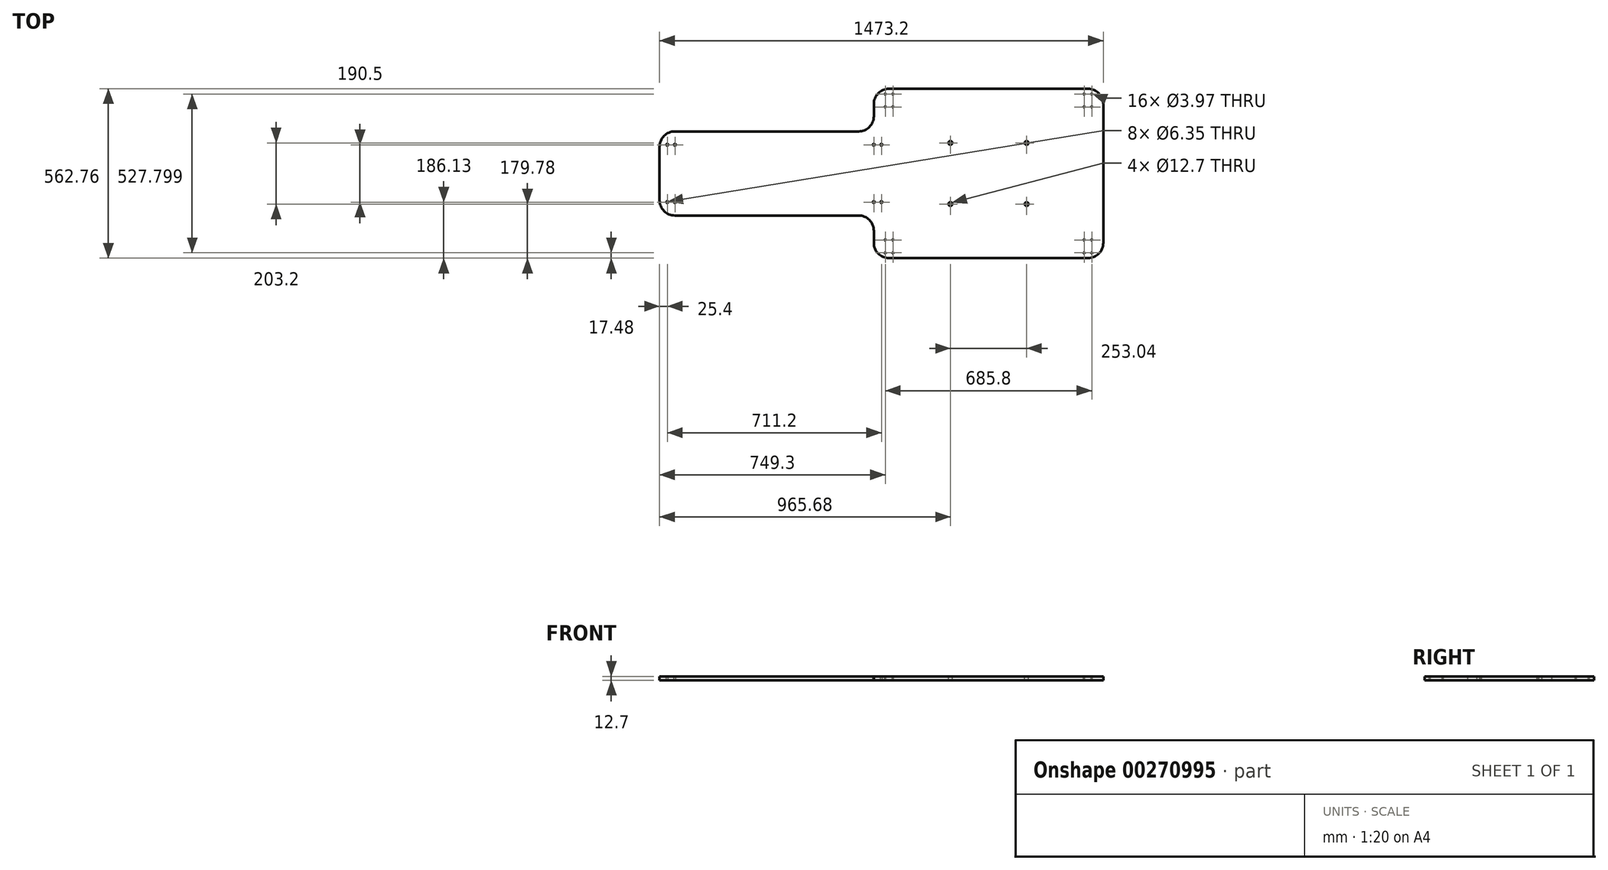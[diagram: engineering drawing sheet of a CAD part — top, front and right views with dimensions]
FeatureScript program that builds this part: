
annotation { "Feature Type Name" : "Feature", "Feature Type Description" : "" }
export const myFeature = defineFeature(function(context is Context, id is Id, definition is map)
    precondition{}
    {
        {
            var Q0;
            Q0=qCreatedBy(makeId("Top.planeOp"),FACE);
            var sketch = newSketch(context, id + "F0", { "sketchPlane" : qUnion([Q0])});
            skLineSegment(sketch, "E0", {"start": v(0, 0) * mm, "end": v(1473.2, 0) * mm, "construction": true});
            skLineSegment(sketch, "E1", {"start": v(1473.2, 0) * mm, "end": v(1473.2, 230.58) * mm});
            skLineSegment(sketch, "E2", {"start": v(1422.4, 281.38) * mm, "end": v(762, 281.38) * mm});
            skLineSegment(sketch, "E3", {"start": v(711.2, 230.58) * mm, "end": v(711.2, 190.5) * mm});
            skLineSegment(sketch, "E4", {"start": v(660.4, 139.7) * mm, "end": v(50.8, 139.7) * mm});
            skLineSegment(sketch, "E5", {"start": v(0, 88.9) * mm, "end": v(0, 0) * mm});
            skPoint(sketch, "E6.visualSharp", {"position": v(0, 139.7) * mm});
            skArc(sketch, "E6.filletArc", {"start": v(50.8, 139.7) * mm, "mid": v(14.88, 124.82) * mm, "end": v(0, 88.9) * mm});
            skPoint(sketch, "E7.visualSharp", {"position": v(711.2, 281.38) * mm});
            skArc(sketch, "E7.filletArc", {"start": v(762, 281.38) * mm, "mid": v(726.08, 266.5) * mm, "end": v(711.2, 230.58) * mm});
            skPoint(sketch, "E8.visualSharp", {"position": v(711.2, 139.7) * mm});
            skArc(sketch, "E8.filletArc", {"start": v(660.4, 139.7) * mm, "mid": v(696.32, 154.58) * mm, "end": v(711.2, 190.5) * mm});
            skPoint(sketch, "E9.visualSharp", {"position": v(1473.2, 281.38) * mm});
            skArc(sketch, "E9.filletArc", {"start": v(1473.2, 230.58) * mm, "mid": v(1458.32, 266.5) * mm, "end": v(1422.4, 281.38) * mm});
            skPoint(sketch, "E10.MirrorP", {"position": v(711.2, -139.7) * mm});
            skPoint(sketch, "E11.MirrorP", {"position": v(711.2, -281.38) * mm});
            skLineSegment(sketch, "E12.MirrorCS", {"start": v(1473.2, 0) * mm, "end": v(1473.2, -230.58) * mm});
            skLineSegment(sketch, "E13.MirrorCS", {"start": v(1422.4, -281.38) * mm, "end": v(762, -281.38) * mm});
            skPoint(sketch, "E14.MirrorP", {"position": v(0, -139.7) * mm});
            skLineSegment(sketch, "E15.MirrorCS", {"start": v(711.2, -230.58) * mm, "end": v(711.2, -190.5) * mm});
            skPoint(sketch, "E16.MirrorP", {"position": v(1473.2, -281.38) * mm});
            skArc(sketch, "E17.MirrorCS", {"start": v(1473.2, -230.58) * mm, "mid": v(1458.32, -266.5) * mm, "end": v(1422.4, -281.38) * mm});
            skLineSegment(sketch, "E18.MirrorCS", {"start": v(0, -88.9) * mm, "end": v(0, 0) * mm});
            skArc(sketch, "E19.MirrorCS", {"start": v(660.4, -139.7) * mm, "mid": v(696.32, -154.58) * mm, "end": v(711.2, -190.5) * mm});
            skLineSegment(sketch, "E20.MirrorCS", {"start": v(660.4, -139.7) * mm, "end": v(50.8, -139.7) * mm});
            skArc(sketch, "E21.MirrorCS", {"start": v(50.8, -139.7) * mm, "mid": v(14.88, -124.82) * mm, "end": v(0, -88.9) * mm});
            skArc(sketch, "E22.MirrorCS", {"start": v(762, -281.38) * mm, "mid": v(726.08, -266.5) * mm, "end": v(711.2, -230.58) * mm});
            skPoint(sketch, "E23", {"position": v(1473.2, 244.48) * mm});
            skLineSegment(sketch, "E24", {"start": v(1473.2, 244.48) * mm, "end": v(1246.97, 244.48) * mm, "construction": true});
            skSolve(sketch);
        }
        {
            var Q0;
            Q0=makeQuery(id+"F0.imprint","IMPRINT",FACE,{"disambiguationData":[TD([[makeQuery(id+"F0.imprint","IMPRINT",EDGE,{"derivedFrom":sQuery(id+"F0.wireOp",EDGE,"E1")}),1.0]])]});
            extrude(context, id + "F1", {"entities" : qUnion([Q0]), "depth" : 12.7 * mm});
        }
        {
            var Q0;
            Q0=makeQuery(id+"F1.opExtrude","CAP_FACE",FACE,{"disambiguationData":[OSD([sQuery(id+"F0.wireOp",EDGE,"E1"),sQuery(id+"F0.wireOp",EDGE,"E2"),sQuery(id+"F0.wireOp",EDGE,"E3"),sQuery(id+"F0.wireOp",EDGE,"E4"),sQuery(id+"F0.wireOp",EDGE,"E5"),sQuery(id+"F0.wireOp",EDGE,"E6.filletArc"),sQuery(id+"F0.wireOp",EDGE,"E7.filletArc"),sQuery(id+"F0.wireOp",EDGE,"E8.filletArc"),sQuery(id+"F0.wireOp",EDGE,"E9.filletArc"),sQuery(id+"F0.wireOp",EDGE,"E12.MirrorCS"),sQuery(id+"F0.wireOp",EDGE,"E13.MirrorCS"),sQuery(id+"F0.wireOp",EDGE,"E15.MirrorCS"),sQuery(id+"F0.wireOp",EDGE,"E17.MirrorCS"),sQuery(id+"F0.wireOp",EDGE,"E18.MirrorCS"),sQuery(id+"F0.wireOp",EDGE,"E19.MirrorCS"),sQuery(id+"F0.wireOp",EDGE,"E20.MirrorCS"),sQuery(id+"F0.wireOp",EDGE,"E21.MirrorCS"),sQuery(id+"F0.wireOp",EDGE,"E22.MirrorCS")])],"isStart":false});
            var sketch = newSketch(context, id + "F2", { "sketchPlane" : qUnion([Q0])});
            skPoint(sketch, "E25", {"position": v(1422.4, -242.47) * mm});
            skLineSegment(sketch, "E26", {"start": v(1400.97, -242.47) * mm, "end": v(1485.34, -242.47) * mm, "construction": true});
            skLineSegment(sketch, "E27", {"start": v(1422.4, -204.1) * mm, "end": v(1422.4, -307.94) * mm, "construction": true});
            skLineSegment(sketch, "E28", {"start": v(1400.97, -217.07) * mm, "end": v(1443.83, -217.07) * mm, "construction": true});
            skLineSegment(sketch, "E29", {"start": v(1400.97, -267.87) * mm, "end": v(1443.83, -267.87) * mm, "construction": true});
            skPoint(sketch, "E30", {"position": v(1435.1, -263.9) * mm});
            skPoint(sketch, "E31.MirrorP", {"position": v(1435.1, -221.04) * mm});
            skPoint(sketch, "E32.MirrorP", {"position": v(1409.7, -221.04) * mm});
            skPoint(sketch, "E33.MirrorP", {"position": v(1409.7, -263.9) * mm});
            skLineSegment(sketch, "E34", {"start": v(1092.2, 339.37) * mm, "end": v(1092.2, -479.33) * mm, "construction": true});
            skLineSegment(sketch, "E35", {"start": v(1473.2, 0) * mm, "end": v(0, 0) * mm, "construction": true});
            skPoint(sketch, "E36.MirrorP", {"position": v(1409.7, 221.04) * mm});
            skPoint(sketch, "E37.MirrorP", {"position": v(1435.1, 221.04) * mm});
            skPoint(sketch, "E38.MirrorP", {"position": v(1435.1, 263.9) * mm});
            skPoint(sketch, "E39.MirrorP", {"position": v(1409.7, 263.9) * mm});
            skPoint(sketch, "E40.MirrorP", {"position": v(774.7, 263.9) * mm});
            skPoint(sketch, "E41.MirrorP", {"position": v(749.3, 263.9) * mm});
            skPoint(sketch, "E42.MirrorP", {"position": v(749.3, 221.04) * mm});
            skPoint(sketch, "E43.MirrorP", {"position": v(774.7, 221.04) * mm});
            skPoint(sketch, "E44.MirrorP", {"position": v(774.7, -221.04) * mm});
            skPoint(sketch, "E45.MirrorP", {"position": v(749.3, -221.04) * mm});
            skPoint(sketch, "E46.MirrorP", {"position": v(749.3, -263.9) * mm});
            skPoint(sketch, "E47.MirrorP", {"position": v(774.7, -263.9) * mm});
            skPoint(sketch, "E48", {"position": v(1218.72, 101.6) * mm});
            skPoint(sketch, "E49.MirrorP", {"position": v(965.68, 101.6) * mm});
            skPoint(sketch, "E50.MirrorP", {"position": v(1218.72, -101.6) * mm});
            skPoint(sketch, "E51.MirrorP", {"position": v(965.68, -101.6) * mm});
            skPoint(sketch, "E52", {"position": v(25.4, 95.25) * mm});
            skPoint(sketch, "E53", {"position": v(50.8, 95.25) * mm});
            skPoint(sketch, "E54.MirrorP", {"position": v(25.4, -95.25) * mm});
            skPoint(sketch, "E55.MirrorP", {"position": v(50.8, -95.25) * mm});
            skLineSegment(sketch, "E56", {"start": v(381, 211.87) * mm, "end": v(381, -230.79) * mm, "construction": true});
            skPoint(sketch, "E57.MirrorP", {"position": v(711.2, 95.25) * mm});
            skPoint(sketch, "E58.MirrorP", {"position": v(736.6, 95.25) * mm});
            skPoint(sketch, "E59.MirrorP", {"position": v(736.6, -95.25) * mm});
            skPoint(sketch, "E60.MirrorP", {"position": v(711.2, -95.25) * mm});
            skSolve(sketch);
        }
        {
            var Q0;
            Q0=sQuery(id+"F2.wireOp",VERTEX,"E41.MirrorP");
            var Q1;
            Q1=sQuery(id+"F2.wireOp",VERTEX,"E40.MirrorP");
            var Q2;
            Q2=sQuery(id+"F2.wireOp",VERTEX,"E43.MirrorP");
            var Q3;
            Q3=sQuery(id+"F2.wireOp",VERTEX,"E42.MirrorP");
            var Q4;
            Q4=sQuery(id+"F2.wireOp",VERTEX,"E45.MirrorP");
            var Q5;
            Q5=sQuery(id+"F2.wireOp",VERTEX,"E44.MirrorP");
            var Q6;
            Q6=sQuery(id+"F2.wireOp",VERTEX,"E47.MirrorP");
            var Q7;
            Q7=sQuery(id+"F2.wireOp",VERTEX,"E46.MirrorP");
            var Q8;
            Q8=sQuery(id+"F2.wireOp",VERTEX,"E32.MirrorP");
            var Q9;
            Q9=sQuery(id+"F2.wireOp",VERTEX,"E31.MirrorP");
            var Q10;
            Q10=sQuery(id+"F2.wireOp",VERTEX,"E30");
            var Q11;
            Q11=sQuery(id+"F2.wireOp",VERTEX,"E33.MirrorP");
            var Q12;
            Q12=sQuery(id+"F2.wireOp",VERTEX,"E37.MirrorP");
            var Q13;
            Q13=sQuery(id+"F2.wireOp",VERTEX,"E36.MirrorP");
            var Q14;
            Q14=sQuery(id+"F2.wireOp",VERTEX,"E39.MirrorP");
            var Q15;
            Q15=sQuery(id+"F2.wireOp",VERTEX,"E38.MirrorP");
            var Q16;
            Q16=makeQuery(id+"F1.opExtrude","SWEPT_BODY",BODY,{"disambiguationData":[OSD([sQuery(id+"F0.wireOp",EDGE,"E1"),sQuery(id+"F0.wireOp",EDGE,"E2"),sQuery(id+"F0.wireOp",EDGE,"E3"),sQuery(id+"F0.wireOp",EDGE,"E4"),sQuery(id+"F0.wireOp",EDGE,"E5"),sQuery(id+"F0.wireOp",EDGE,"E6.filletArc"),sQuery(id+"F0.wireOp",EDGE,"E7.filletArc"),sQuery(id+"F0.wireOp",EDGE,"E8.filletArc"),sQuery(id+"F0.wireOp",EDGE,"E9.filletArc"),sQuery(id+"F0.wireOp",EDGE,"E12.MirrorCS"),sQuery(id+"F0.wireOp",EDGE,"E13.MirrorCS"),sQuery(id+"F0.wireOp",EDGE,"E15.MirrorCS"),sQuery(id+"F0.wireOp",EDGE,"E17.MirrorCS"),sQuery(id+"F0.wireOp",EDGE,"E18.MirrorCS"),sQuery(id+"F0.wireOp",EDGE,"E19.MirrorCS"),sQuery(id+"F0.wireOp",EDGE,"E20.MirrorCS"),sQuery(id+"F0.wireOp",EDGE,"E21.MirrorCS"),sQuery(id+"F0.wireOp",EDGE,"E22.MirrorCS")])]});
            hole(context, id + "F3", {"style" : HoleStyle.SIMPLE, "endStyle" : HoleEndStyle.THROUGH, "holeDiameter" : 3.97 * mm, "tappedDepth" : 12.7 * mm, "tapClearance" : 3, "locations" : qUnion([Q0, Q1, Q2, Q3, Q4, Q5, Q6, Q7, Q8, Q9, Q10, Q11, Q12, Q13, Q14, Q15]), "scope" : qUnion([Q16])});
        }
        {
            var Q0;
            Q0=sQuery(id+"F2.wireOp",VERTEX,"E49.MirrorP");
            var Q1;
            Q1=sQuery(id+"F2.wireOp",VERTEX,"E48");
            var Q2;
            Q2=sQuery(id+"F2.wireOp",VERTEX,"E50.MirrorP");
            var Q3;
            Q3=sQuery(id+"F2.wireOp",VERTEX,"E51.MirrorP");
            var Q4;
            Q4=makeQuery(id+"F1.opExtrude","SWEPT_BODY",BODY,{"disambiguationData":[OSD([sQuery(id+"F0.wireOp",EDGE,"E1"),sQuery(id+"F0.wireOp",EDGE,"E2"),sQuery(id+"F0.wireOp",EDGE,"E3"),sQuery(id+"F0.wireOp",EDGE,"E4"),sQuery(id+"F0.wireOp",EDGE,"E5"),sQuery(id+"F0.wireOp",EDGE,"E6.filletArc"),sQuery(id+"F0.wireOp",EDGE,"E7.filletArc"),sQuery(id+"F0.wireOp",EDGE,"E8.filletArc"),sQuery(id+"F0.wireOp",EDGE,"E9.filletArc"),sQuery(id+"F0.wireOp",EDGE,"E12.MirrorCS"),sQuery(id+"F0.wireOp",EDGE,"E13.MirrorCS"),sQuery(id+"F0.wireOp",EDGE,"E15.MirrorCS"),sQuery(id+"F0.wireOp",EDGE,"E17.MirrorCS"),sQuery(id+"F0.wireOp",EDGE,"E18.MirrorCS"),sQuery(id+"F0.wireOp",EDGE,"E19.MirrorCS"),sQuery(id+"F0.wireOp",EDGE,"E20.MirrorCS"),sQuery(id+"F0.wireOp",EDGE,"E21.MirrorCS"),sQuery(id+"F0.wireOp",EDGE,"E22.MirrorCS")])]});
            hole(context, id + "F4", {"style" : HoleStyle.SIMPLE, "endStyle" : HoleEndStyle.THROUGH, "holeDiameter" : 12.7 * mm, "tappedDepth" : 12.7 * mm, "tapClearance" : 3, "locations" : qUnion([Q0, Q1, Q2, Q3]), "scope" : qUnion([Q4])});
        }
        {
            var Q0;
            Q0=sQuery(id+"F2.wireOp",VERTEX,"E52");
            var Q1;
            Q1=sQuery(id+"F2.wireOp",VERTEX,"E53");
            var Q2;
            Q2=sQuery(id+"F2.wireOp",VERTEX,"E55.MirrorP");
            var Q3;
            Q3=sQuery(id+"F2.wireOp",VERTEX,"E54.MirrorP");
            var Q4;
            Q4=sQuery(id+"F2.wireOp",VERTEX,"E57.MirrorP");
            var Q5;
            Q5=sQuery(id+"F2.wireOp",VERTEX,"E58.MirrorP");
            var Q6;
            Q6=sQuery(id+"F2.wireOp",VERTEX,"E59.MirrorP");
            var Q7;
            Q7=sQuery(id+"F2.wireOp",VERTEX,"E60.MirrorP");
            var Q8;
            Q8=makeQuery(id+"F1.opExtrude","SWEPT_BODY",BODY,{"disambiguationData":[OSD([sQuery(id+"F0.wireOp",EDGE,"E1"),sQuery(id+"F0.wireOp",EDGE,"E2"),sQuery(id+"F0.wireOp",EDGE,"E3"),sQuery(id+"F0.wireOp",EDGE,"E4"),sQuery(id+"F0.wireOp",EDGE,"E5"),sQuery(id+"F0.wireOp",EDGE,"E6.filletArc"),sQuery(id+"F0.wireOp",EDGE,"E7.filletArc"),sQuery(id+"F0.wireOp",EDGE,"E8.filletArc"),sQuery(id+"F0.wireOp",EDGE,"E9.filletArc"),sQuery(id+"F0.wireOp",EDGE,"E12.MirrorCS"),sQuery(id+"F0.wireOp",EDGE,"E13.MirrorCS"),sQuery(id+"F0.wireOp",EDGE,"E15.MirrorCS"),sQuery(id+"F0.wireOp",EDGE,"E17.MirrorCS"),sQuery(id+"F0.wireOp",EDGE,"E18.MirrorCS"),sQuery(id+"F0.wireOp",EDGE,"E19.MirrorCS"),sQuery(id+"F0.wireOp",EDGE,"E20.MirrorCS"),sQuery(id+"F0.wireOp",EDGE,"E21.MirrorCS"),sQuery(id+"F0.wireOp",EDGE,"E22.MirrorCS")])]});
            hole(context, id + "F5", {"style" : HoleStyle.SIMPLE, "endStyle" : HoleEndStyle.THROUGH, "holeDiameter" : 6.35 * mm, "tappedDepth" : 12.7 * mm, "tapClearance" : 3, "locations" : qUnion([Q0, Q1, Q2, Q3, Q4, Q5, Q6, Q7]), "scope" : qUnion([Q8])});
        }
    });
